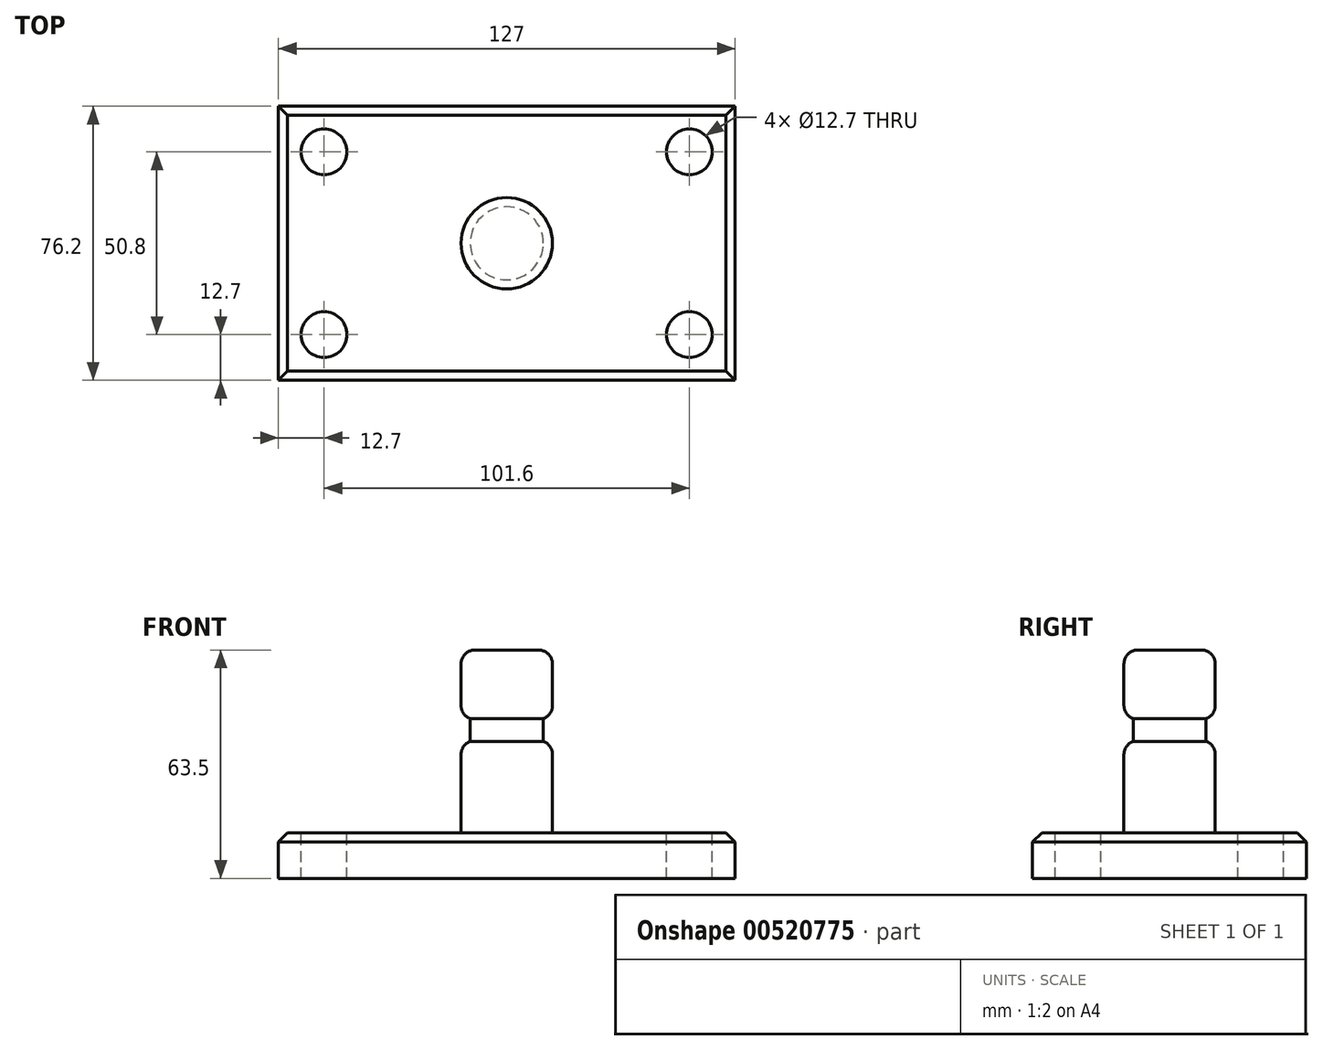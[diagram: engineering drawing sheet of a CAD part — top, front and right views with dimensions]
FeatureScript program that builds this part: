
annotation { "Feature Type Name" : "Feature", "Feature Type Description" : "" }
export const myFeature = defineFeature(function(context is Context, id is Id, definition is map)
    precondition{}
    {
        {
            var Q0;
            Q0=qCreatedBy(makeId("Top.planeOp"),FACE);
            var sketch = newSketch(context, id + "F0", { "sketchPlane" : qUnion([Q0])});
            skLineSegment(sketch, "E0.bottom", {"start": v(-63.5, 38.1) * mm, "end": v(63.5, 38.1) * mm});
            skLineSegment(sketch, "E0.top", {"start": v(-63.5, -38.1) * mm, "end": v(63.5, -38.1) * mm});
            skLineSegment(sketch, "E0.left", {"start": v(-63.5, 38.1) * mm, "end": v(-63.5, -38.1) * mm});
            skLineSegment(sketch, "E0.right", {"start": v(63.5, 38.1) * mm, "end": v(63.5, -38.1) * mm});
            skPoint(sketch, "E0.middle", {"position": v(0, 0) * mm});
            skSolve(sketch);
        }
        {
            var Q0;
            Q0=makeQuery(id+"F0.imprint","IMPRINT",FACE,{"disambiguationData":[TD([[makeQuery(id+"F0.imprint","IMPRINT",EDGE,{"derivedFrom":sQuery(id+"F0.wireOp",EDGE,"E0.bottom")}),-1.0]])]});
            extrude(context, id + "F1", {"entities" : qUnion([Q0]), "depth" : 12.7 * mm, "offsetDistance" : 25.4 * mm});
        }
        {
            var Q0;
            Q0=makeQuery(id+"F1.opExtrude","CAP_FACE",FACE,{"disambiguationData":[OSD([sQuery(id+"F0.wireOp",EDGE,"E0.bottom"),sQuery(id+"F0.wireOp",EDGE,"E0.top"),sQuery(id+"F0.wireOp",EDGE,"E0.left"),sQuery(id+"F0.wireOp",EDGE,"E0.right")])],"isStart":false});
            var sketch = newSketch(context, id + "F2", { "sketchPlane" : qUnion([Q0])});
            skPoint(sketch, "E1.middle", {"position": v(0, 0) * mm});
            skCircle(sketch, "E2", {"center": v(-50.8, 25.4) * mm, "radius": 6.35 * mm});
            skCircle(sketch, "E3", {"center": v(-50.8, -25.4) * mm, "radius": 6.35 * mm});
            skCircle(sketch, "E4", {"center": v(50.8, -25.4) * mm, "radius": 6.35 * mm});
            skCircle(sketch, "E5", {"center": v(50.8, 25.4) * mm, "radius": 6.35 * mm});
            skSolve(sketch);
        }
        {
            var Q0;
            Q0=makeQuery(id+"F2.imprint","IMPRINT",FACE,{"disambiguationData":[TD([[makeQuery(id+"F2.imprint","IMPRINT",EDGE,{"derivedFrom":sQuery(id+"F2.wireOp",EDGE,"E2")}),1.0]])]});
            var Q1;
            Q1=makeQuery(id+"F2.imprint","IMPRINT",FACE,{"disambiguationData":[TD([[makeQuery(id+"F2.imprint","IMPRINT",EDGE,{"derivedFrom":sQuery(id+"F2.wireOp",EDGE,"E3")}),1.0]])]});
            var Q2;
            Q2=makeQuery(id+"F2.imprint","IMPRINT",FACE,{"disambiguationData":[TD([[makeQuery(id+"F2.imprint","IMPRINT",EDGE,{"derivedFrom":sQuery(id+"F2.wireOp",EDGE,"E4")}),1.0]])]});
            var Q3;
            Q3=makeQuery(id+"F2.imprint","IMPRINT",FACE,{"disambiguationData":[TD([[makeQuery(id+"F2.imprint","IMPRINT",EDGE,{"derivedFrom":sQuery(id+"F2.wireOp",EDGE,"E5")}),1.0]])]});
            var Q4;
            Q4=makeQuery(id+"F1.opExtrude","CAP_FACE",FACE,{"disambiguationData":[OSD([sQuery(id+"F0.wireOp",EDGE,"E0.bottom"),sQuery(id+"F0.wireOp",EDGE,"E0.top"),sQuery(id+"F0.wireOp",EDGE,"E0.left"),sQuery(id+"F0.wireOp",EDGE,"E0.right")])],"isStart":true});
            extrude(context, id + "F3", {"entities" : qUnion([Q0, Q1, Q2, Q3]), "operationType" : NewBodyOperationType.REMOVE, "endBound" : BoundingType.UP_TO_SURFACE, "oppositeDirection" : true, "depth" : 25.4 * mm, "endBoundEntityFace" : qUnion([Q4]), "offsetDistance" : 25.4 * mm});
        }
        {
            var Q0;
            Q0=qCreatedBy(makeId("Front.planeOp"),FACE);
            var sketch = newSketch(context, id + "F4", { "sketchPlane" : qUnion([Q0])});
            skLineSegment(sketch, "E6.bottom", {"start": v(0, 12.7) * mm, "end": v(12.7, 12.7) * mm});
            skLineSegment(sketch, "E6.top", {"start": v(0, 63.5) * mm, "end": v(12.7, 63.5) * mm});
            skLineSegment(sketch, "E6.left", {"start": v(0, 12.7) * mm, "end": v(0, 63.5) * mm});
            skLineSegment(sketch, "E6.right", {"start": v(12.7, 12.7) * mm, "end": v(12.7, 63.5) * mm});
            skSolve(sketch);
        }
        {
            var Q0;
            Q0=makeQuery(id+"F4.imprint","IMPRINT",FACE,{"disambiguationData":[TD([[makeQuery(id+"F4.imprint","IMPRINT",EDGE,{"derivedFrom":sQuery(id+"F4.wireOp",EDGE,"E6.bottom")}),1.0]])]});
            var Q1;
            Q1=sQuery(id+"F4.wireOp",EDGE,"E6.left");
            revolve(context, id + "F5", {"operationType" : NewBodyOperationType.ADD, "entities" : qUnion([Q0]), "axis" : qUnion([Q1]), "revolveType" : RevolveType.FULL});
        }
        {
            var Q0;
            Q0=qCreatedBy(makeId("Front.planeOp"),FACE);
            var sketch = newSketch(context, id + "F6", { "sketchPlane" : qUnion([Q0])});
            skLineSegment(sketch, "E7.bottom", {"start": v(17.26, 44.45) * mm, "end": v(10.16, 44.45) * mm});
            skLineSegment(sketch, "E7.top", {"start": v(17.26, 38.1) * mm, "end": v(10.16, 38.1) * mm});
            skLineSegment(sketch, "E7.left", {"start": v(17.26, 44.45) * mm, "end": v(17.26, 38.1) * mm});
            skLineSegment(sketch, "E7.right", {"start": v(10.16, 44.45) * mm, "end": v(10.16, 38.1) * mm});
            skSolve(sketch);
        }
        {
            var Q0;
            Q0=makeQuery(id+"F6.imprint","IMPRINT",FACE,{"disambiguationData":[TD([[makeQuery(id+"F6.imprint","IMPRINT",EDGE,{"derivedFrom":sQuery(id+"F6.wireOp",EDGE,"E7.bottom")}),1.0]])]});
            var Q1;
            Q1=makeQuery(id+"F5.opRevolve","SWEPT_FACE",FACE,{"disambiguationData":[OSD([sQuery(id+"F4.wireOp",EDGE,"E6.right")])]});
            revolve(context, id + "F7", {"operationType" : NewBodyOperationType.REMOVE, "entities" : qUnion([Q0]), "axis" : qUnion([Q1]), "revolveType" : RevolveType.FULL, "oppositeDirection" : true});
        }
        {
            var Q0;
            Q0=makeQuery(id+"F5.opRevolve","SWEPT_EDGE",EDGE,{"disambiguationData":[OSD([sQuery(id+"F4.wireOp",EDGE,"E6.bottom"),sQuery(id+"F4.wireOp",EDGE,"E6.right")])]});
            var Q1;
            Q1=makeQuery(id+"F7.boolean.opBoolean","INTERSECT",EDGE,{"derivedFrom":[makeQuery(id+"F5.opRevolve","SWEPT_FACE",FACE,{"disambiguationData":[OSD([sQuery(id+"F4.wireOp",EDGE,"E6.right")])]}),makeQuery(id+"F7.opRevolve","SWEPT_FACE",FACE,{"disambiguationData":[OSD([sQuery(id+"F6.wireOp",EDGE,"E7.top")])]})]});
            var Q2;
            Q2=makeQuery(id+"F7.boolean.opBoolean","INTERSECT",EDGE,{"derivedFrom":[makeQuery(id+"F5.opRevolve","SWEPT_FACE",FACE,{"disambiguationData":[OSD([sQuery(id+"F4.wireOp",EDGE,"E6.right")])]}),makeQuery(id+"F7.opRevolve","SWEPT_FACE",FACE,{"disambiguationData":[OSD([sQuery(id+"F6.wireOp",EDGE,"E7.bottom")])]})]});
            var Q3;
            Q3=makeQuery(id+"F5.opRevolve","SWEPT_EDGE",EDGE,{"disambiguationData":[OSD([sQuery(id+"F4.wireOp",EDGE,"E6.top"),sQuery(id+"F4.wireOp",EDGE,"E6.right")])]});
            fillet(context, id + "F8", {"entities" : qUnion([Q0, Q1, Q2, Q3]), "radius" : 3.8 * mm, "tangentPropagation" : true, "allowEdgeOverflow" : false});
        }
        {
            var Q0;
            Q0=makeQuery(id+"F1.opExtrude","CAP_EDGE",EDGE,{"disambiguationData":[OSD([sQuery(id+"F0.wireOp",EDGE,"E0.top")])],"isStart":false});
            var Q1;
            Q1=makeQuery(id+"F1.opExtrude","CAP_EDGE",EDGE,{"disambiguationData":[OSD([sQuery(id+"F0.wireOp",EDGE,"E0.left")])],"isStart":false});
            var Q2;
            Q2=makeQuery(id+"F1.opExtrude","CAP_EDGE",EDGE,{"disambiguationData":[OSD([sQuery(id+"F0.wireOp",EDGE,"E0.right")])],"isStart":false});
            var Q3;
            Q3=makeQuery(id+"F1.opExtrude","CAP_EDGE",EDGE,{"disambiguationData":[OSD([sQuery(id+"F0.wireOp",EDGE,"E0.bottom")])],"isStart":false});
            chamfer(context, id + "F9", {"entities" : qUnion([Q0, Q1, Q2, Q3]), "width" : 2.54 * mm, "tangentPropagation" : true});
        }
    });
